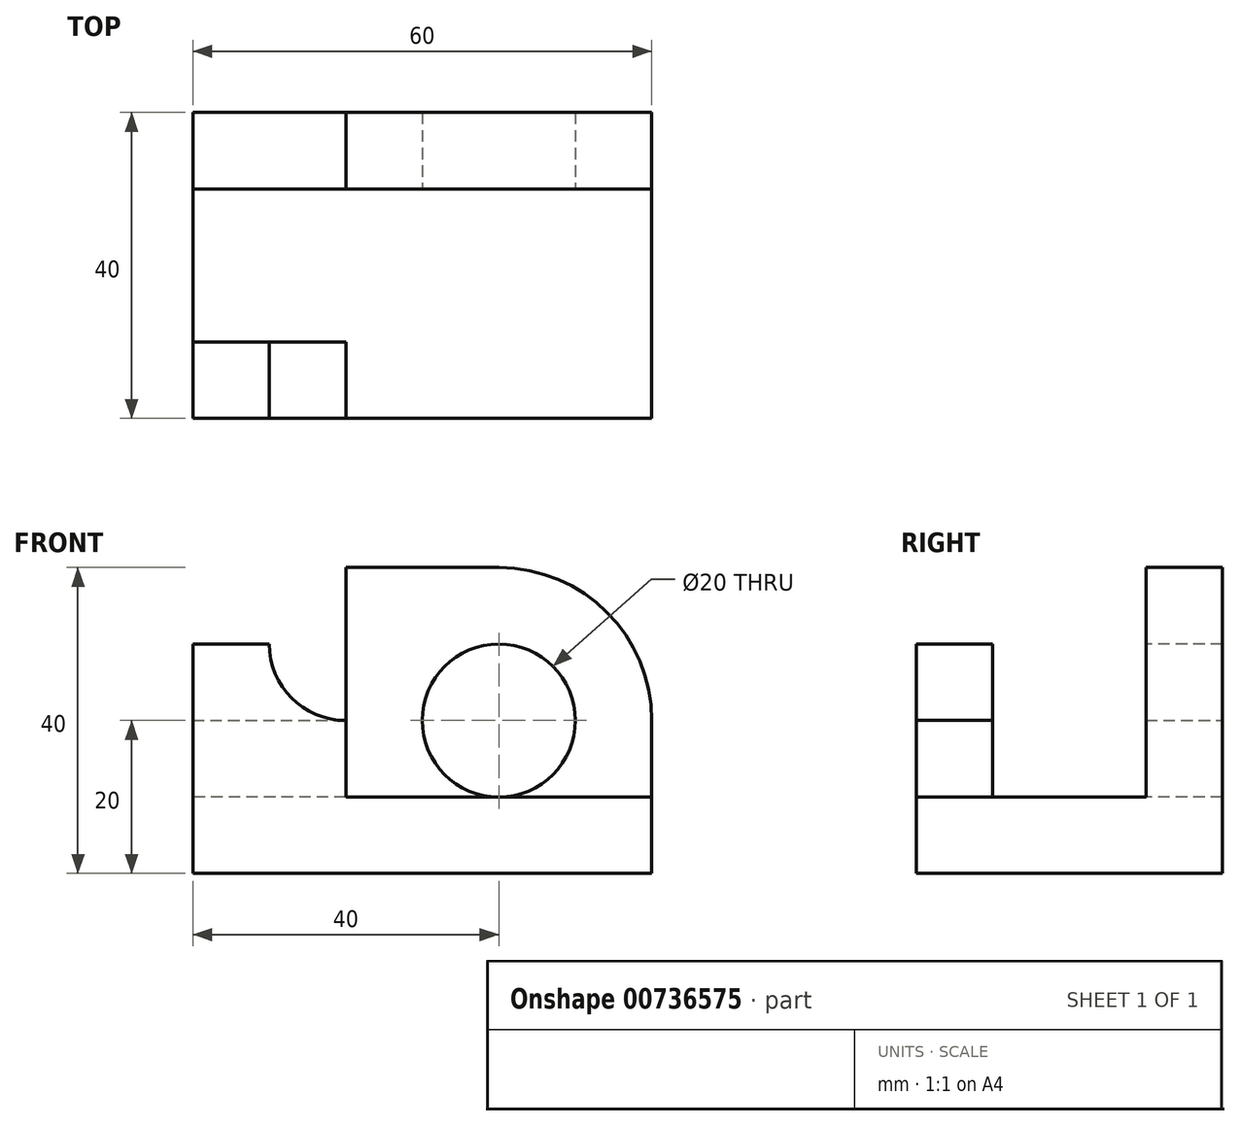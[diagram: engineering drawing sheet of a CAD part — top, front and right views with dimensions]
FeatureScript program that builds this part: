
annotation { "Feature Type Name" : "Feature", "Feature Type Description" : "" }
export const myFeature = defineFeature(function(context is Context, id is Id, definition is map)
    precondition{}
    {
        {
            var Q0;
            Q0=qCreatedBy(makeId("Top.planeOp"),FACE);
            var sketch = newSketch(context, id + "F0", { "sketchPlane" : qUnion([Q0])});
            skLineSegment(sketch, "E0", {"start": v(0, 0) * mm, "end": v(60, 0) * mm});
            skLineSegment(sketch, "E1", {"start": v(60, 0) * mm, "end": v(60, 40) * mm});
            skLineSegment(sketch, "E2", {"start": v(60, 40) * mm, "end": v(0, 40) * mm});
            skLineSegment(sketch, "E3", {"start": v(0, 40) * mm, "end": v(0, 0) * mm});
            skSolve(sketch);
        }
        {
            var Q0;
            Q0 = qSketchRegion(id + "F0", true);
            extrude(context, id + "F1", {"entities" : qUnion([Q0]), "depth" : 40 * mm, "offsetDistance" : 25 * mm});
        }
        {
            var Q0;
            Q0=makeQuery(id+"F1.opExtrude","CAP_FACE",FACE,{"disambiguationData":[OSD([sQuery(id+"F0.wireOp",EDGE,"E0"),sQuery(id+"F0.wireOp",EDGE,"E1"),sQuery(id+"F0.wireOp",EDGE,"E2"),sQuery(id+"F0.wireOp",EDGE,"E3")])],"isStart":false});
            var sketch = newSketch(context, id + "F2", { "sketchPlane" : qUnion([Q0])});
            skLineSegment(sketch, "E4", {"start": v(0, 40) * mm, "end": v(0, 30) * mm});
            skLineSegment(sketch, "E5", {"start": v(0, 30) * mm, "end": v(0, 10) * mm});
            skLineSegment(sketch, "E6", {"start": v(0, 10) * mm, "end": v(60, 10) * mm});
            skLineSegment(sketch, "E7", {"start": v(60, 10) * mm, "end": v(60, 30) * mm});
            skLineSegment(sketch, "E8", {"start": v(60, 30) * mm, "end": v(0, 30) * mm});
            skLineSegment(sketch, "E9", {"start": v(0, 40) * mm, "end": v(20, 40) * mm});
            skLineSegment(sketch, "E10", {"start": v(20, 40) * mm, "end": v(20, 30) * mm});
            skLineSegment(sketch, "E11", {"start": v(20, 30) * mm, "end": v(0, 30) * mm});
            skSolve(sketch);
        }
        {
            var Q0;
            Q0=makeQuery(id+"F2.imprint","IMPRINT",FACE,{"disambiguationData":[TD([[makeQuery(id+"F2.imprint","IMPRINT",EDGE,{"derivedFrom":sQuery(id+"F2.wireOp",EDGE,"E4")}),1.0]])]});
            extrude(context, id + "F3", {"entities" : qUnion([Q0]), "operationType" : NewBodyOperationType.REMOVE, "oppositeDirection" : true, "depth" : 10 * mm, "offsetDistance" : 25 * mm});
        }
        {
            var Q0;
            Q0=makeQuery(id+"F2.imprint","IMPRINT",FACE,{"disambiguationData":[TD([[makeQuery(id+"F2.imprint","IMPRINT",EDGE,{"derivedFrom":sQuery(id+"F2.wireOp",EDGE,"E5")}),1.0]])]});
            extrude(context, id + "F4", {"entities" : qUnion([Q0]), "operationType" : NewBodyOperationType.REMOVE, "oppositeDirection" : true, "depth" : 30 * mm, "offsetDistance" : 25 * mm});
        }
        {
            var Q0;
            Q0=makeQuery(id+"F1.opExtrude","SWEPT_FACE",FACE,{"disambiguationData":[OSD([sQuery(id+"F0.wireOp",EDGE,"E0")])]});
            var sketch = newSketch(context, id + "F5", { "sketchPlane" : qUnion([Q0])});
            skLineSegment(sketch, "E12.bottom", {"start": v(0, 40) * mm, "end": v(60, 40) * mm});
            skLineSegment(sketch, "E12.top", {"start": v(0, 30) * mm, "end": v(60, 30) * mm});
            skLineSegment(sketch, "E12.left", {"start": v(0, 40) * mm, "end": v(0, 30) * mm});
            skLineSegment(sketch, "E12.right", {"start": v(60, 40) * mm, "end": v(60, 30) * mm});
            skSolve(sketch);
        }
        {
            var Q0;
            Q0=makeQuery(id+"F5.imprint","IMPRINT",FACE,{"disambiguationData":[TD([[makeQuery(id+"F5.imprint","IMPRINT",EDGE,{"derivedFrom":sQuery(id+"F5.wireOp",EDGE,"E12.bottom")}),-1.0]])]});
            extrude(context, id + "F6", {"entities" : qUnion([Q0]), "operationType" : NewBodyOperationType.REMOVE, "oppositeDirection" : true, "depth" : 10 * mm, "offsetDistance" : 25 * mm});
        }
        {
            var Q0;
            Q0=makeQuery(id+"F1.opExtrude","SWEPT_FACE",FACE,{"disambiguationData":[OSD([sQuery(id+"F0.wireOp",EDGE,"E0")])]});
            var sketch = newSketch(context, id + "F7", { "sketchPlane" : qUnion([Q0])});
            skLineSegment(sketch, "E13.bottom", {"start": v(60, 30) * mm, "end": v(20, 30) * mm});
            skLineSegment(sketch, "E13.top", {"start": v(60, 10) * mm, "end": v(20, 10) * mm});
            skLineSegment(sketch, "E13.left", {"start": v(60, 30) * mm, "end": v(60, 10) * mm});
            skLineSegment(sketch, "E13.right", {"start": v(20, 30) * mm, "end": v(20, 10) * mm});
            skSolve(sketch);
        }
        {
            var Q0;
            Q0=makeQuery(id+"F7.imprint","IMPRINT",FACE,{"disambiguationData":[TD([[makeQuery(id+"F7.imprint","IMPRINT",EDGE,{"derivedFrom":sQuery(id+"F7.wireOp",EDGE,"E13.bottom")}),-1.0]])]});
            extrude(context, id + "F8", {"entities" : qUnion([Q0]), "operationType" : NewBodyOperationType.REMOVE, "oppositeDirection" : true, "depth" : 10 * mm, "offsetDistance" : 25 * mm});
        }
        {
            var Q0;
            Q0=makeQuery(id+"F1.opExtrude","SWEPT_FACE",FACE,{"disambiguationData":[OSD([sQuery(id+"F0.wireOp",EDGE,"E0")])]});
            var sketch = newSketch(context, id + "F9", { "sketchPlane" : qUnion([Q0])});
            skLineSegment(sketch, "E14", {"start": v(20, 10) * mm, "end": v(20, 20) * mm});
            skLineSegment(sketch, "E15", {"start": v(20, 20) * mm, "end": v(10, 20) * mm});
            skLineSegment(sketch, "E16", {"start": v(10, 20) * mm, "end": v(10, 30) * mm});
            skArc(sketch, "E17", {"start": v(10, 30) * mm, "mid": v(12.93, 22.93) * mm, "end": v(20, 20) * mm});
            skSolve(sketch);
        }
        {
            var Q0;
            {var subQ0=sQuery(id+"F9.wireOp",EDGE,"E17");Q0=makeQuery(id+"F9.imprint","IMPRINT",FACE,{"disambiguationData":[TD([[makeQuery(id+"F9.imprint","IMPRINT",EDGE,{"derivedFrom":subQ0}),1.0]])]});}
            extrude(context, id + "F10", {"entities" : qUnion([Q0]), "operationType" : NewBodyOperationType.REMOVE, "oppositeDirection" : true, "depth" : 10 * mm, "offsetDistance" : 25 * mm});
        }
        {
            var Q0;
            Q0=makeQuery(id+"F1.opExtrude","SWEPT_FACE",FACE,{"disambiguationData":[OSD([sQuery(id+"F0.wireOp",EDGE,"E2")])]});
            var sketch = newSketch(context, id + "F11", { "sketchPlane" : qUnion([Q0])});
            skLineSegment(sketch, "E18.bottom", {"start": v(0, 30) * mm, "end": v(-20, 30) * mm});
            skLineSegment(sketch, "E18.top", {"start": v(0, 20) * mm, "end": v(-20, 20) * mm});
            skLineSegment(sketch, "E18.left", {"start": v(0, 30) * mm, "end": v(0, 20) * mm});
            skLineSegment(sketch, "E18.right", {"start": v(-20, 30) * mm, "end": v(-20, 20) * mm});
            skSolve(sketch);
        }
        {
            var Q0;
            Q0 = qSketchRegion(id + "F11", true);
            extrude(context, id + "F12", {"entities" : qUnion([Q0]), "operationType" : NewBodyOperationType.REMOVE, "oppositeDirection" : true, "depth" : 10 * mm, "offsetDistance" : 25 * mm});
        }
        {
            var Q0;
            Q0=makeQuery(id+"F4.boolean.opBoolean","COPY",FACE,{"derivedFrom":makeQuery(id+"F4.opExtrude","SWEPT_FACE",FACE,{"disambiguationData":[OSD([sQuery(id+"F2.wireOp",EDGE,"E8"),sQuery(id+"F2.wireOp",EDGE,"E11")])]})});
            var sketch = newSketch(context, id + "F13", { "sketchPlane" : qUnion([Q0])});
            skLineSegment(sketch, "E19", {"start": v(60, 10) * mm, "end": v(60, 20) * mm});
            skLineSegment(sketch, "E20", {"start": v(60, 20) * mm, "end": v(40, 20) * mm});
            skLineSegment(sketch, "E21", {"start": v(40, 20) * mm, "end": v(20, 20) * mm});
            skCircle(sketch, "E22", {"center": v(40, 20) * mm, "radius": 10 * mm});
            skArc(sketch, "E23", {"start": v(60, 20) * mm, "mid": v(40, 40) * mm, "end": v(20, 20) * mm});
            skSolve(sketch);
        }
        {
            var Q0;
            {var subQ0=sQuery(id+"F13.wireOp",EDGE,"E21");var subQ1=sQuery(id+"F13.wireOp",EDGE,"E20");var subQ2=makeQuery(id+"F13.imprint","INTERSECT",VERTEX,{"derivedFrom":[subQ1,subQ0]});Q0=makeQuery(id+"F13.imprint","IMPRINT",FACE,{"disambiguationData":[TD([[makeQuery(id+"F13.imprint","IMPRINT",EDGE,{"disambiguationData":[TD([[subQ2,1.0]])],"derivedFrom":subQ1}),-1.0]])]});}
            var Q1;
            {var subQ0=sQuery(id+"F13.wireOp",EDGE,"E21");var subQ1=sQuery(id+"F13.wireOp",EDGE,"E20");var subQ2=makeQuery(id+"F13.imprint","INTERSECT",VERTEX,{"derivedFrom":[subQ1,subQ0]});Q1=makeQuery(id+"F13.imprint","IMPRINT",FACE,{"disambiguationData":[TD([[makeQuery(id+"F13.imprint","IMPRINT",EDGE,{"disambiguationData":[TD([[subQ2,1.0]])],"derivedFrom":subQ1}),1.0]])]});}
            var Q2;
            {var subQ0=sQuery(id+"F13.wireOp",EDGE,"E23");var subQ1=sQuery(id+"F2.wireOp",EDGE,"E8");var subQ4=makeQuery(id+"F4.boolean.opBoolean","COPY",EDGE,{"derivedFrom":makeQuery(id+"F4.opExtrude","CAP_EDGE",EDGE,{"disambiguationData":[OSD([subQ1,sQuery(id+"F2.wireOp",EDGE,"E11")])],"isStart":true})});var subQ5=makeQuery(id+"F13.imprint","INTERSECT",VERTEX,{"derivedFrom":[subQ4,subQ0]});Q2=makeQuery(id+"F13.imprint","IMPRINT",FACE,{"disambiguationData":[TD([[makeQuery(id+"F13.imprint","IMPRINT",EDGE,{"disambiguationData":[TD([[subQ5,1.0]])],"derivedFrom":subQ0}),-1.0]])]});}
            var Q3;
            {var subQ1=sQuery(id+"F2.wireOp",EDGE,"E11");var subQ2=sQuery(id+"F2.wireOp",EDGE,"E8");var subQ3=makeQuery(id+"F12.boolean.opBoolean","MERGE",EDGE,{"derivedFrom":[makeQuery(id+"F3.boolean.opBoolean","COPY",EDGE,{"derivedFrom":makeQuery(id+"F3.opExtrude","SWEPT_EDGE",EDGE,{"disambiguationData":[OSD([subQ2,sQuery(id+"F2.wireOp",EDGE,"E10"),subQ1])]})}),makeQuery(id+"F12.opExtrude","CAP_EDGE",EDGE,{"disambiguationData":[OSD([sQuery(id+"F11.wireOp",EDGE,"E18.right")])],"isStart":false})]});Q3=makeQuery(id+"F13.imprint","IMPRINT",FACE,{"disambiguationData":[TD([[makeQuery(id+"F13.imprint","IMPRINT",EDGE,{"derivedFrom":subQ3}),-1.0]])]});}
            extrude(context, id + "F14", {"entities" : qUnion([Q0, Q1, Q2, Q3]), "operationType" : NewBodyOperationType.REMOVE, "oppositeDirection" : true, "depth" : 10 * mm, "offsetDistance" : 25 * mm});
        }
    });
